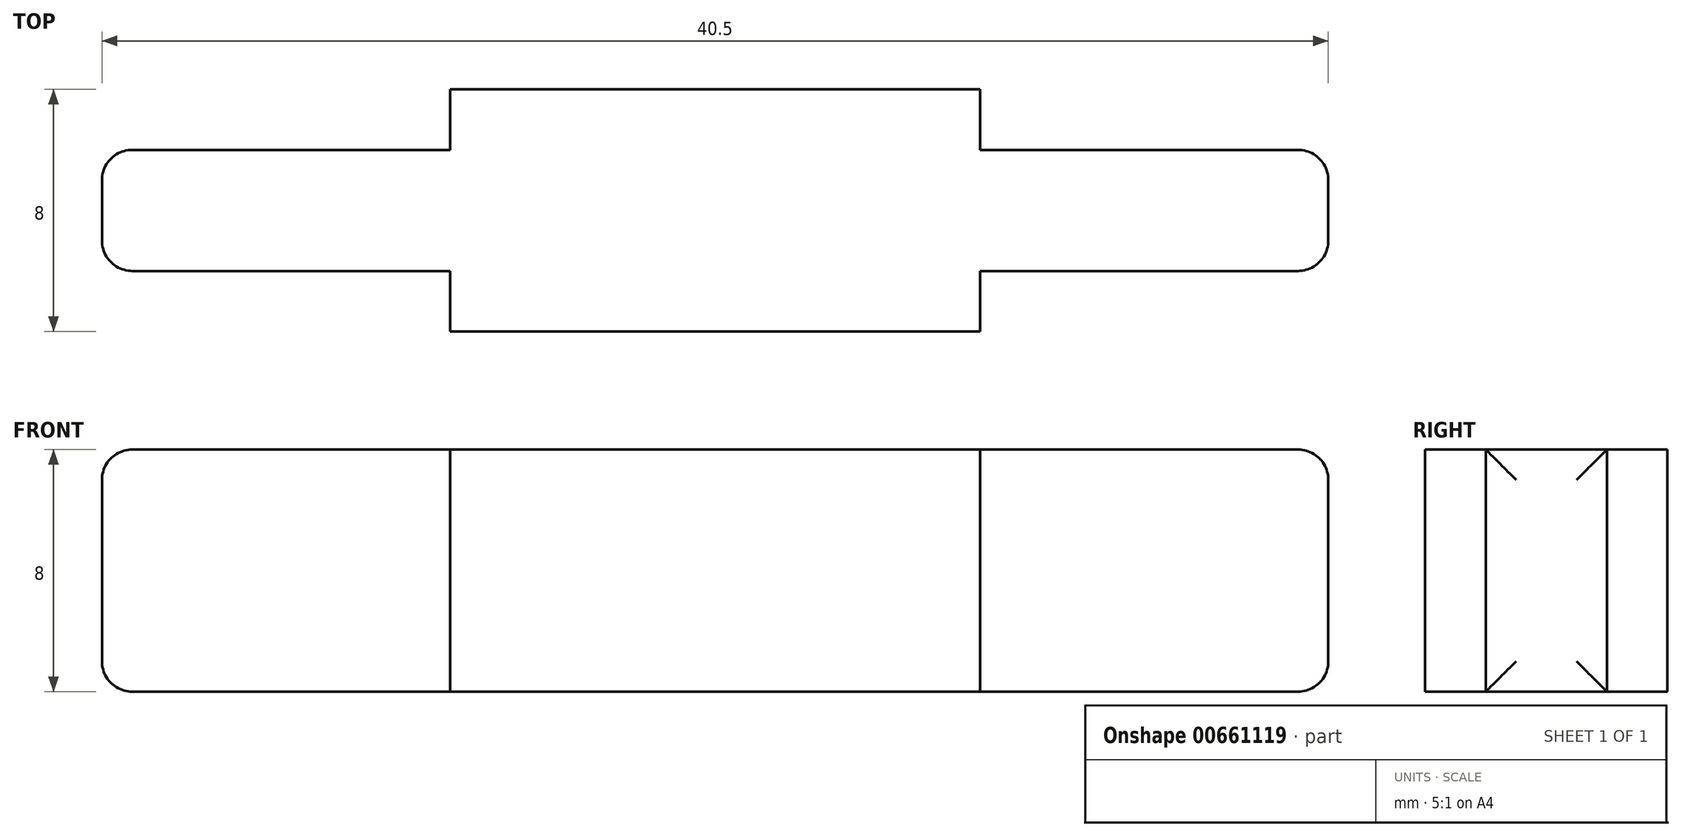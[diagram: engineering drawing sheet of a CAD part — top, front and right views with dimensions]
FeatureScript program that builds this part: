
annotation { "Feature Type Name" : "Feature", "Feature Type Description" : "" }
export const myFeature = defineFeature(function(context is Context, id is Id, definition is map)
    precondition{}
    {
        {
            var Q0;
            Q0=qCreatedBy(makeId("Top.planeOp"),FACE);
            var sketch = newSketch(context, id + "F0", { "sketchPlane" : qUnion([Q0])});
            skLineSegment(sketch, "E0.bottom", {"start": v(20.25, 2) * mm, "end": v(-20.25, 2) * mm});
            skLineSegment(sketch, "E0.top", {"start": v(20.25, -2) * mm, "end": v(-20.25, -2) * mm});
            skLineSegment(sketch, "E0.left", {"start": v(20.25, 2) * mm, "end": v(20.25, -2) * mm});
            skLineSegment(sketch, "E0.right", {"start": v(-20.25, 2) * mm, "end": v(-20.25, -2) * mm});
            skPoint(sketch, "E0.middle", {"position": v(0, 0) * mm});
            skLineSegment(sketch, "E1.bottom", {"start": v(8.75, 4) * mm, "end": v(-8.75, 4) * mm});
            skLineSegment(sketch, "E1.top", {"start": v(8.75, -4) * mm, "end": v(-8.75, -4) * mm});
            skLineSegment(sketch, "E1.left", {"start": v(8.75, 4) * mm, "end": v(8.75, -4) * mm});
            skLineSegment(sketch, "E1.right", {"start": v(-8.75, 4) * mm, "end": v(-8.75, -4) * mm});
            skSolve(sketch);
        }
        {
            var Q0;
            Q0 = qSketchRegion(id + "F0", true);
            extrude(context, id + "F1", {"entities" : qUnion([Q0]), "depth" : 8 * mm, "offsetDistance" : 25 * mm});
        }
        {
            var Q0;
            Q0=makeQuery(id+"F1.opExtrude","SWEPT_EDGE",EDGE,{"disambiguationData":[OSD([sQuery(id+"F0.wireOp",EDGE,"E0.top"),sQuery(id+"F0.wireOp",EDGE,"E0.right")])]});
            var Q1;
            Q1=makeQuery(id+"F1.opExtrude","CAP_EDGE",EDGE,{"disambiguationData":[OSD([sQuery(id+"F0.wireOp",EDGE,"E0.right")])],"isStart":false});
            var Q2;
            Q2=makeQuery(id+"F1.opExtrude","CAP_EDGE",EDGE,{"disambiguationData":[OSD([sQuery(id+"F0.wireOp",EDGE,"E0.right")])],"isStart":true});
            var Q3;
            Q3=makeQuery(id+"F1.opExtrude","SWEPT_EDGE",EDGE,{"disambiguationData":[OSD([sQuery(id+"F0.wireOp",EDGE,"E0.bottom"),sQuery(id+"F0.wireOp",EDGE,"E0.right")])]});
            var Q4;
            Q4=makeQuery(id+"F1.opExtrude","CAP_EDGE",EDGE,{"disambiguationData":[OSD([sQuery(id+"F0.wireOp",EDGE,"E0.left")])],"isStart":false});
            var Q5;
            Q5=makeQuery(id+"F1.opExtrude","SWEPT_EDGE",EDGE,{"disambiguationData":[OSD([sQuery(id+"F0.wireOp",EDGE,"E0.bottom"),sQuery(id+"F0.wireOp",EDGE,"E0.left")])]});
            var Q6;
            Q6=makeQuery(id+"F1.opExtrude","CAP_EDGE",EDGE,{"disambiguationData":[OSD([sQuery(id+"F0.wireOp",EDGE,"E0.left")])],"isStart":true});
            var Q7;
            Q7=makeQuery(id+"F1.opExtrude","SWEPT_EDGE",EDGE,{"disambiguationData":[OSD([sQuery(id+"F0.wireOp",EDGE,"E0.top"),sQuery(id+"F0.wireOp",EDGE,"E0.left")])]});
            fillet(context, id + "F2", {"entities" : qUnion([Q0, Q1, Q2, Q3, Q4, Q5, Q6, Q7]), "radius" : 1 * mm, "tangentPropagation" : true, "allowEdgeOverflow" : false});
        }
    });
